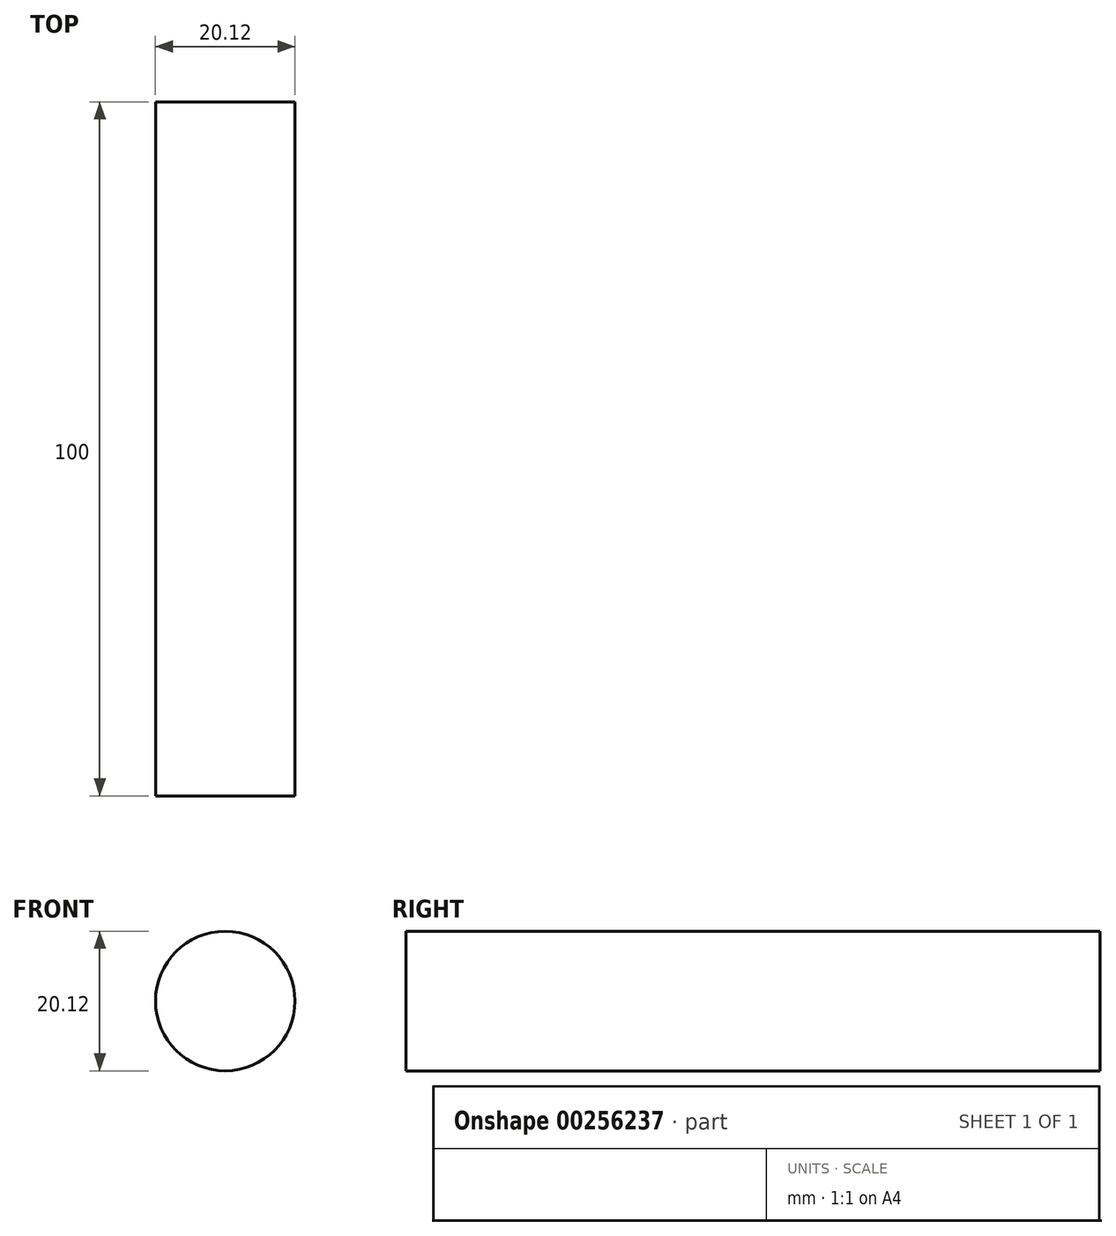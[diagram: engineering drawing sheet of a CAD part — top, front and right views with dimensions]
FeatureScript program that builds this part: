
annotation { "Feature Type Name" : "Feature", "Feature Type Description" : "" }
export const myFeature = defineFeature(function(context is Context, id is Id, definition is map)
    precondition{}
    {
        {
            var Q0;
            Q0=qCreatedBy(makeId("Front.planeOp"),FACE);
            var sketch = newSketch(context, id + "F0", { "sketchPlane" : qUnion([Q0])});
            skCircle(sketch, "E0", {"center": v(0, 0) * mm, "radius": 10.06 * mm});
            skSolve(sketch);
        }
        {
            var Q0;
            Q0 = qSketchRegion(id + "F0", true);
            extrude(context, id + "F1", {"entities" : qUnion([Q0]), "depth" : 100 * mm});
        }
    });
